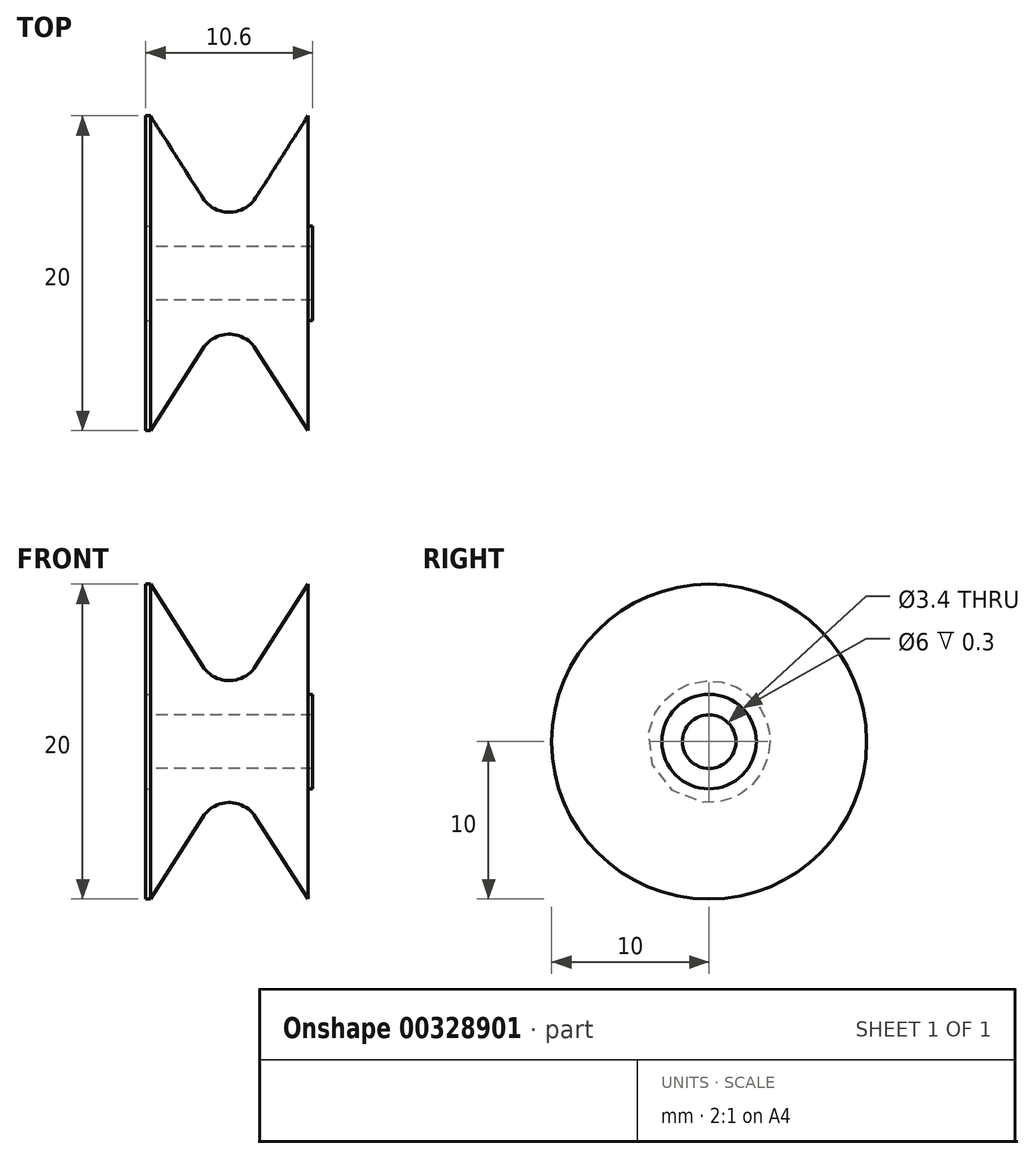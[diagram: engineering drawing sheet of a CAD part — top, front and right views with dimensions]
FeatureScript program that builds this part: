
annotation { "Feature Type Name" : "Feature", "Feature Type Description" : "" }
export const myFeature = defineFeature(function(context is Context, id is Id, definition is map)
    precondition{}
    {
        {
            var Q0;
            Q0=qCreatedBy(makeId("Front.planeOp"),FACE);
            var sketch = newSketch(context, id + "F0", { "sketchPlane" : qUnion([Q0])});
            skLineSegment(sketch, "E0", {"start": v(-5, 1.7) * mm, "end": v(-5, 10) * mm});
            skLineSegment(sketch, "E1", {"start": v(-5, 10) * mm, "end": v(-1.69, 4.8) * mm});
            skLineSegment(sketch, "E2", {"start": v(0, -6.23) * mm, "end": v(0, 31.01) * mm, "construction": true});
            skLineSegment(sketch, "E3.MirrorCS", {"start": v(5, 1.7) * mm, "end": v(5, 10) * mm});
            skLineSegment(sketch, "E4.MirrorCS", {"start": v(5, 10) * mm, "end": v(1.69, 4.8) * mm});
            skLineSegment(sketch, "E5", {"start": v(5, 1.7) * mm, "end": v(-5, 1.7) * mm});
            skLineSegment(sketch, "E6", {"start": v(0, 0) * mm, "end": v(-27.05, 0) * mm, "construction": true});
            skPoint(sketch, "E7.visualSharp", {"position": v(0, 2.15) * mm});
            skArc(sketch, "E7.filletArc", {"start": v(-1.69, 4.8) * mm, "mid": v(0, 3.87) * mm, "end": v(1.69, 4.8) * mm});
            skSolve(sketch);
        }
        {
            var Q0;
            Q0=qCreatedBy(makeId("Right.planeOp"),FACE);
            var sketch = newSketch(context, id + "F1", { "sketchPlane" : qUnion([Q0])});
            skCircle(sketch, "E8", {"center": v(0, 0) * mm, "radius": 67.05 * mm});
            skSolve(sketch);
        }
        {
            var Q0;
            Q0=makeQuery(id+"F0.imprint","IMPRINT",FACE,{"disambiguationData":[TD([[makeQuery(id+"F0.imprint","IMPRINT",EDGE,{"derivedFrom":sQuery(id+"F0.wireOp",EDGE,"E0")}),-1.0]])]});
            var Q1;
            Q1=sQuery(id+"F1.wireOp",EDGE,"E8");
            revolve(context, id + "F2", {"entities" : qUnion([Q0]), "axis" : qUnion([Q1]), "revolveType" : RevolveType.FULL});
        }
        {
            var Q0;
            Q0=makeQuery(id+"F2.opRevolve","SWEPT_BODY",BODY,{"disambiguationData":[OSD([sQuery(id+"F0.wireOp",EDGE,"E0"),sQuery(id+"F0.wireOp",EDGE,"E1"),sQuery(id+"F0.wireOp",EDGE,"E3.MirrorCS"),sQuery(id+"F0.wireOp",EDGE,"E4.MirrorCS"),sQuery(id+"F0.wireOp",EDGE,"E5")])]});
            var Q1;
            Q1=sQuery(id+"F0.wireOp",EDGE,"E6");
            transform(context, id + "F3", {"entities" : qUnion([Q0]), "transformType" : TransformType.ROTATION, "transformAxis" : qUnion([Q1]), "angle" : 90 * degree, "makeCopy" : false});
        }
        {
            var Q0;
            Q0=makeQuery(id+"F2.opRevolve","SWEPT_FACE",FACE,{"disambiguationData":[OSD([sQuery(id+"F0.wireOp",EDGE,"E3.MirrorCS")])]});
            var sketch = newSketch(context, id + "F4", { "sketchPlane" : qUnion([Q0])});
            skCircle(sketch, "E9", {"center": v(0, 0) * mm, "radius": 3 * mm});
            skSolve(sketch);
        }
        {
            var Q0;
            Q0=makeQuery(id+"F4.imprint","IMPRINT",FACE,{"disambiguationData":[TD([[makeQuery(id+"F4.imprint","IMPRINT",EDGE,{"derivedFrom":sQuery(id+"F4.wireOp",EDGE,"E9")}),1.0]])]});
            extrude(context, id + "F5", {"entities" : qUnion([Q0]), "operationType" : NewBodyOperationType.ADD, "depth" : 0.3 * mm});
        }
        {
            var Q0;
            Q0=makeQuery(id+"F2.opRevolve","SWEPT_FACE",FACE,{"disambiguationData":[OSD([sQuery(id+"F0.wireOp",EDGE,"E0")])]});
            var sketch = newSketch(context, id + "F6", { "sketchPlane" : qUnion([Q0])});
            skCircle(sketch, "E10.0", {"center": v(0, 0) * mm, "radius": 3 * mm});
            skSolve(sketch);
        }
        {
            var Q0;
            Q0=makeQuery(id+"F6.imprint","IMPRINT",FACE,{"disambiguationData":[TD([[makeQuery(id+"F6.imprint","IMPRINT",EDGE,{"derivedFrom":sQuery(id+"F6.wireOp",EDGE,"E10.0")}),-1.0]])]});
            extrude(context, id + "F7", {"entities" : qUnion([Q0]), "operationType" : NewBodyOperationType.ADD, "depth" : 0.3 * mm});
        }
    });
